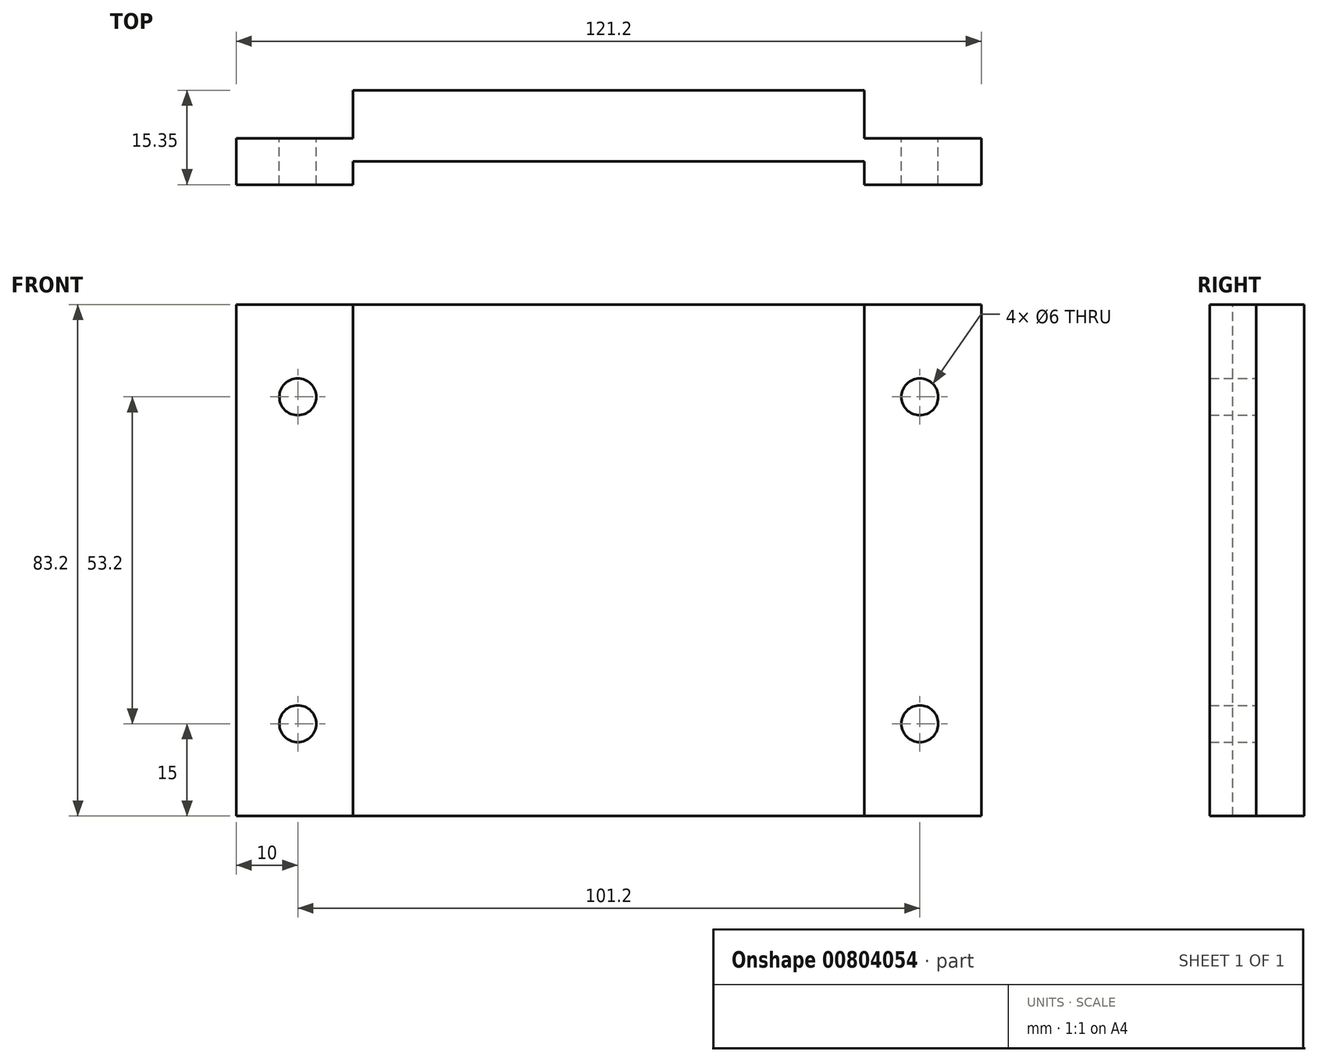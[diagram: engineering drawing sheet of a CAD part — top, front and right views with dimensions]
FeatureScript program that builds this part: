
annotation { "Feature Type Name" : "Feature", "Feature Type Description" : "" }
export const myFeature = defineFeature(function(context is Context, id is Id, definition is map)
    precondition{}
    {
        {
            var Q0;
            Q0=qCreatedBy(makeId("Front.planeOp"),FACE);
            var sketch = newSketch(context, id + "F0", { "sketchPlane" : qUnion([Q0])});
            skLineSegment(sketch, "E0.bottom", {"start": v(0, 0) * mm, "end": v(-83.2, 0) * mm});
            skLineSegment(sketch, "E0.top", {"start": v(0, 83.2) * mm, "end": v(-83.2, 83.2) * mm});
            skLineSegment(sketch, "E0.left", {"start": v(0, 0) * mm, "end": v(0, 83.2) * mm});
            skLineSegment(sketch, "E0.right", {"start": v(-83.2, 0) * mm, "end": v(-83.2, 83.2) * mm});
            skPoint(sketch, "E1.oppositeSnap0", {"position": v(-41.6, 0) * mm});
            skLineSegment(sketch, "E1.bottom", {"start": v(0, 83.2) * mm, "end": v(19, 83.2) * mm});
            skLineSegment(sketch, "E1.top", {"start": v(0, 0) * mm, "end": v(19, 0) * mm});
            skLineSegment(sketch, "E1.left", {"start": v(0, 83.2) * mm, "end": v(0, 0) * mm});
            skLineSegment(sketch, "E1.right", {"start": v(19, 83.2) * mm, "end": v(19, 0) * mm});
            skLineSegment(sketch, "E2.bottom", {"start": v(-83.2, 83.2) * mm, "end": v(-102.2, 83.2) * mm});
            skLineSegment(sketch, "E2.top", {"start": v(-83.2, 0) * mm, "end": v(-102.2, 0) * mm});
            skLineSegment(sketch, "E2.left", {"start": v(-83.2, 83.2) * mm, "end": v(-83.2, 0) * mm});
            skLineSegment(sketch, "E2.right", {"start": v(-102.2, 83.2) * mm, "end": v(-102.2, 0) * mm});
            skPoint(sketch, "E3", {"position": v(-92.2, 68.2) * mm});
            skPoint(sketch, "E4", {"position": v(-92.2, 15) * mm});
            skPoint(sketch, "E5", {"position": v(9, 15) * mm});
            skPoint(sketch, "E6", {"position": v(9, 68.2) * mm});
            skCircle(sketch, "E7", {"center": v(-92.2, 68.2) * mm, "radius": 3 * mm});
            skCircle(sketch, "E8", {"center": v(-92.2, 15) * mm, "radius": 3 * mm});
            skCircle(sketch, "E9", {"center": v(9, 68.2) * mm, "radius": 3 * mm});
            skCircle(sketch, "E10", {"center": v(9, 15) * mm, "radius": 3 * mm});
            skSolve(sketch);
        }
        {
            var Q0;
            Q0=makeQuery(id+"F0.imprint","IMPRINT",FACE,{"disambiguationData":[TD([[makeQuery(id+"F0.imprint","IMPRINT",EDGE,{"derivedFrom":sQuery(id+"F0.wireOp",EDGE,"E0.bottom")}),-1.0]])]});
            extrude(context, id + "F1", {"entities" : qUnion([Q0]), "oppositeDirection" : true, "depth" : 11.58 * mm, "offsetDistance" : 25 * mm});
        }
        {
            var Q0;
            Q0=makeQuery(id+"F0.imprint","IMPRINT",FACE,{"disambiguationData":[TD([[makeQuery(id+"F0.imprint","IMPRINT",EDGE,{"derivedFrom":sQuery(id+"F0.wireOp",EDGE,"E2.bottom")}),1.0]])]});
            var Q1;
            Q1=makeQuery(id+"F0.imprint","IMPRINT",FACE,{"disambiguationData":[TD([[makeQuery(id+"F0.imprint","IMPRINT",EDGE,{"derivedFrom":sQuery(id+"F0.wireOp",EDGE,"E1.bottom")}),-1.0]])]});
            extrude(context, id + "F2", {"entities" : qUnion([Q0, Q1]), "operationType" : NewBodyOperationType.ADD, "endBound" : BoundingType.SYMMETRIC, "depth" : 7.54 * mm, "offsetDistance" : 25 * mm});
        }
    });
